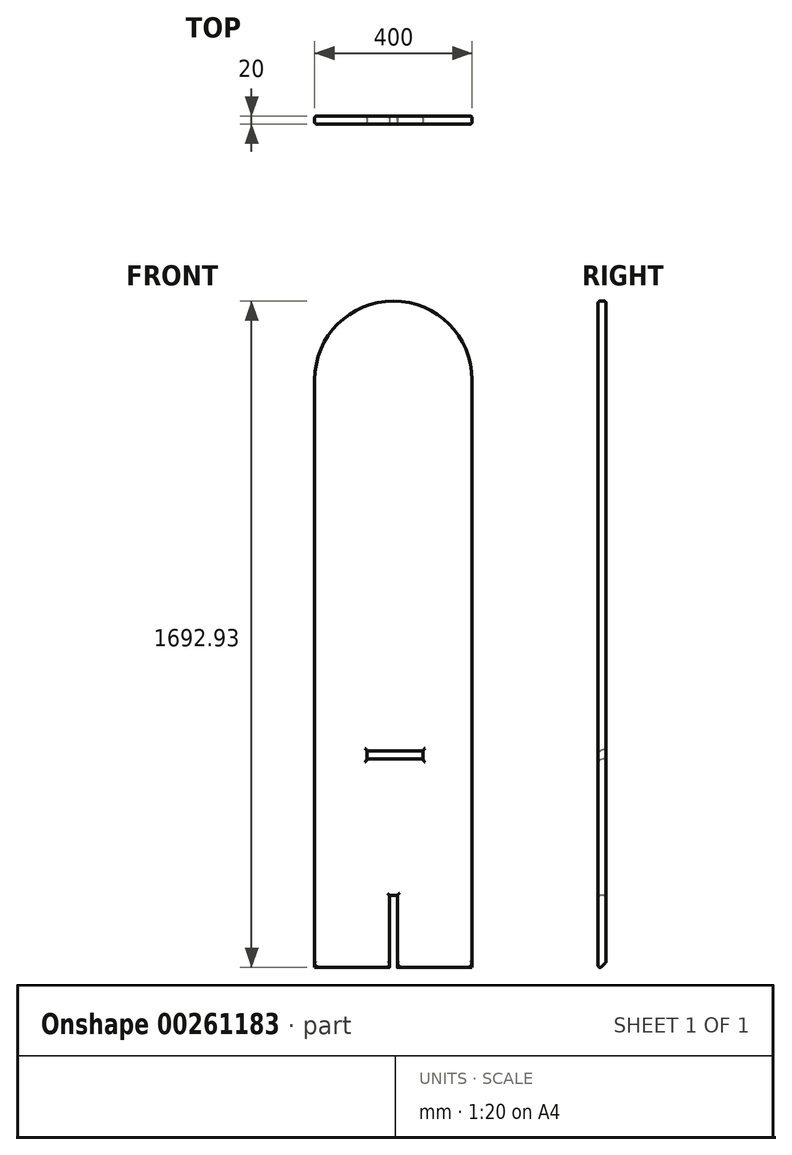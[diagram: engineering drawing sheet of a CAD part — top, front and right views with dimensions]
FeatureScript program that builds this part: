
annotation { "Feature Type Name" : "Feature", "Feature Type Description" : "" }
export const myFeature = defineFeature(function(context is Context, id is Id, definition is map)
    precondition{}
    {
        {
            var Q0;
            Q0=qCreatedBy(makeId("Front.planeOp"),FACE);
            var sketch = newSketch(context, id + "F0", { "sketchPlane" : qUnion([Q0])});
            skLineSegment(sketch, "E0.top", {"start": v(-200, 0) * mm, "end": v(200, 0) * mm});
            skLineSegment(sketch, "E0.left", {"start": v(-200, 1500) * mm, "end": v(-200, 0) * mm});
            skLineSegment(sketch, "E0.right", {"start": v(200, 1500) * mm, "end": v(200, 0) * mm});
            skArc(sketch, "E1", {"start": v(200, 1500) * mm, "mid": v(0, 1700) * mm, "end": v(-200, 1500) * mm});
            skSolve(sketch);
        }
        {
            var Q0;
            Q0 = qSketchRegion(id + "F0", true);
            extrude(context, id + "F1", {"entities" : qUnion([Q0]), "depth" : 20 * mm});
        }
        {
            var Q0;
            Q0=makeQuery(id+"F1.opExtrude","CAP_FACE",FACE,{"disambiguationData":[OSD([sQuery(id+"F0.wireOp",EDGE,"E0.bottom"),sQuery(id+"F0.wireOp",EDGE,"E0.top"),sQuery(id+"F0.wireOp",EDGE,"E0.left"),sQuery(id+"F0.wireOp",EDGE,"E0.right")])],"isStart":false});
            var sketch = newSketch(context, id + "F2", { "sketchPlane" : qUnion([Q0])});
            skLineSegment(sketch, "E2.bottom", {"start": v(-10, 190) * mm, "end": v(10, 190) * mm});
            skLineSegment(sketch, "E2.top", {"start": v(-10, 0) * mm, "end": v(10, 0) * mm});
            skLineSegment(sketch, "E2.left", {"start": v(10, 190) * mm, "end": v(10, 0) * mm});
            skLineSegment(sketch, "E2.right", {"start": v(-10, 190) * mm, "end": v(-10, 0) * mm});
            skSolve(sketch);
        }
        {
            var Q0;
            Q0 = qSketchRegion(id + "F2", true);
            extrude(context, id + "F3", {"entities" : qUnion([Q0]), "operationType" : NewBodyOperationType.REMOVE, "endBound" : BoundingType.UP_TO_NEXT, "oppositeDirection" : true, "depth" : 25 * mm});
        }
        {
            var Q0;
            Q0=makeQuery(id+"FoYhQ1TU8DJVv0B_1.boolean.opBoolean","COPY",EDGE,{"derivedFrom":makeQuery(id+"FoYhQ1TU8DJVv0B_1.opExtrude","CAP_EDGE",EDGE,{"disambiguationData":[OSD([sQuery(id+"F58LfYSewZg3qyR_1.wireOp",EDGE,"nRlcXL84-SfgG-Kv0Z-YoKo-R1KxIp85ui7P.bottom")])],"isStart":true})});
            var Q1;
            {var subQ0=sQuery(id+"F0.wireOp",EDGE,"E0.right");var subQ1=sQuery(id+"F0.wireOp",EDGE,"E0.top");Q1=makeQuery(id+"F3.boolean.opBoolean","SPLIT",EDGE,{"disambiguationData":[TD([makeQuery(id+"F1.opExtrude","SWEPT_FACE",FACE,{"disambiguationData":[OSD([subQ0])]})])],"derivedFrom":makeQuery(id+"F1.opExtrude","CAP_EDGE",EDGE,{"disambiguationData":[OSD([subQ1])],"isStart":false})});}
            cPlane(context, id + "F4", {"entities" : qUnion([Q0, Q1]), "cplaneType" : CPlaneType.LINE_ANGLE, "offset" : 25 * mm, "angle" : 20 * degree, "width" : 150 * mm, "height" : 150 * mm});
        }
        {
            var Q0;
            {var subQ0=sQuery(id+"F0.wireOp",EDGE,"E0.left");var subQ1=sQuery(id+"F0.wireOp",EDGE,"E0.top");Q0=makeQuery(id+"F3.boolean.opBoolean","SPLIT",EDGE,{"disambiguationData":[TD([makeQuery(id+"F1.opExtrude","SWEPT_FACE",FACE,{"disambiguationData":[OSD([subQ0])]})])],"derivedFrom":makeQuery(id+"F1.opExtrude","CAP_EDGE",EDGE,{"disambiguationData":[OSD([subQ1])],"isStart":true})});}
            var Q1;
            {var subQ0=sQuery(id+"F0.wireOp",EDGE,"E0.right");var subQ1=sQuery(id+"F0.wireOp",EDGE,"E0.top");Q1=makeQuery(id+"F3.boolean.opBoolean","SPLIT",EDGE,{"disambiguationData":[TD([makeQuery(id+"F1.opExtrude","SWEPT_FACE",FACE,{"disambiguationData":[OSD([subQ0])]})])],"derivedFrom":makeQuery(id+"F1.opExtrude","CAP_EDGE",EDGE,{"disambiguationData":[OSD([subQ1])],"isStart":true})});}
            chamfer(context, id + "F5", {"entities" : qUnion([Q0, Q1]), "width" : 20 * mm, "tangentPropagation" : true});
        }
        {
            var Q0;
            Q0=qCreatedBy(id+"F4.planeOp",FACE);
            var sketch = newSketch(context, id + "F6", { "sketchPlane" : qUnion([Q0])});
            skLineSegment(sketch, "E3.bottom", {"start": v(-75, 528.84) * mm, "end": v(67, 528.84) * mm});
            skLineSegment(sketch, "E3.top", {"start": v(-75, 506.84) * mm, "end": v(67, 506.84) * mm});
            skLineSegment(sketch, "E3.left", {"start": v(-75, 528.84) * mm, "end": v(-75, 506.84) * mm});
            skLineSegment(sketch, "E3.right", {"start": v(67, 528.84) * mm, "end": v(67, 506.84) * mm});
            skPoint(sketch, "E4", {"position": v(-4, 506.84) * mm});
            skSolve(sketch);
        }
        {
            var Q0;
            Q0 = qSketchRegion(id + "F6", true);
            extrude(context, id + "F7", {"entities" : qUnion([Q0]), "operationType" : NewBodyOperationType.REMOVE, "endBound" : BoundingType.THROUGH_ALL, "depth" : 25 * mm});
        }
        {
            var Q0;
            Q0=makeQuery(id+"F1.opExtrude","CAP_FACE",FACE,{"disambiguationData":[OSD([sQuery(id+"F0.wireOp",EDGE,"E0.bottom"),sQuery(id+"F0.wireOp",EDGE,"E0.top"),sQuery(id+"F0.wireOp",EDGE,"E0.left"),sQuery(id+"F0.wireOp",EDGE,"E0.right")])],"isStart":false});
            var Q1;
            Q1=makeQuery(id+"F1.opExtrude","CAP_FACE",FACE,{"disambiguationData":[OSD([sQuery(id+"F0.wireOp",EDGE,"E0.bottom"),sQuery(id+"F0.wireOp",EDGE,"E0.top"),sQuery(id+"F0.wireOp",EDGE,"E0.left"),sQuery(id+"F0.wireOp",EDGE,"E0.right")])],"isStart":true});
            fillet(context, id + "F8", {"entities" : qUnion([Q0, Q1]), "radius" : 5 * mm, "tangentPropagation" : true, "allowEdgeOverflow" : false});
        }
    });
